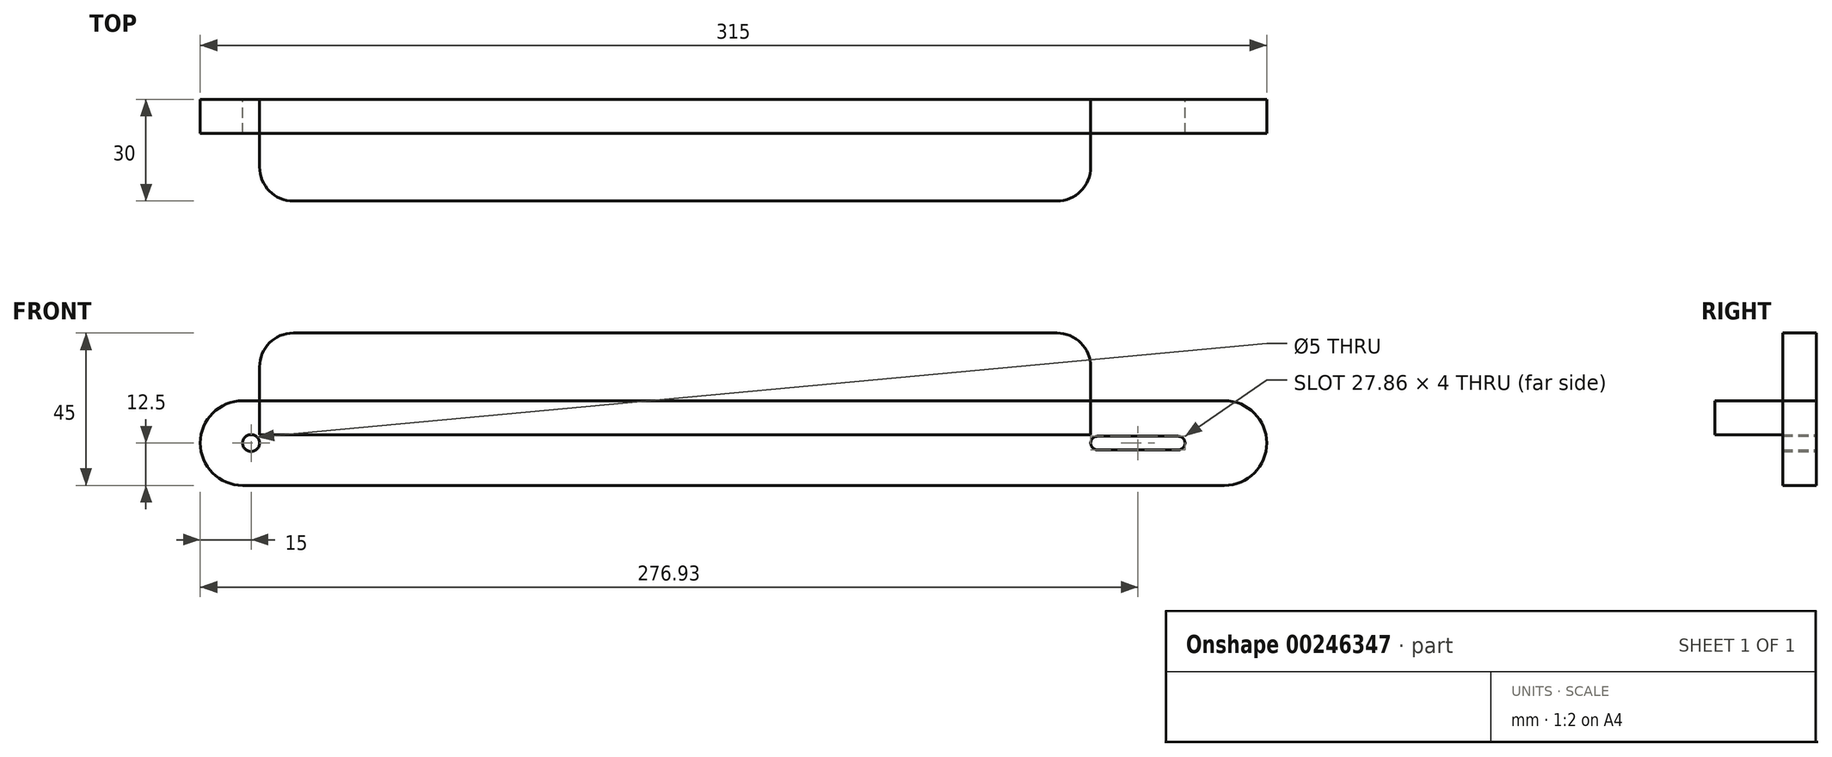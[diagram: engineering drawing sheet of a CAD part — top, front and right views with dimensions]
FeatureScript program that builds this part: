
annotation { "Feature Type Name" : "Feature", "Feature Type Description" : "" }
export const myFeature = defineFeature(function(context is Context, id is Id, definition is map)
    precondition{}
    {
        {
            var Q0;
            Q0=qCreatedBy(makeId("Front.planeOp"),FACE);
            var sketch = newSketch(context, id + "F0", { "sketchPlane" : qUnion([Q0])});
            skLineSegment(sketch, "E0.top", {"start": v(10, 25) * mm, "end": v(325, 25) * mm});
            skLineSegment(sketch, "E0.right", {"start": v(325, 0) * mm, "end": v(325, 25) * mm});
            skCircle(sketch, "E1", {"center": v(25, 12.5) * mm, "radius": 2.5 * mm});
            skArc(sketch, "E2", {"start": v(298.86, 10.5) * mm, "mid": v(300.86, 12.5) * mm, "end": v(298.86, 14.5) * mm});
            skArc(sketch, "E3", {"start": v(275, 14.5) * mm, "mid": v(273, 12.5) * mm, "end": v(275, 10.5) * mm});
            skLineSegment(sketch, "E4", {"start": v(275, 14.5) * mm, "end": v(298.86, 14.5) * mm});
            skLineSegment(sketch, "E5", {"start": v(298.86, 10.5) * mm, "end": v(275, 10.5) * mm});
            skLineSegment(sketch, "E6", {"start": v(325, 0) * mm, "end": v(10, 0) * mm});
            skLineSegment(sketch, "E7", {"start": v(10, 0) * mm, "end": v(10, 25) * mm});
            skSolve(sketch);
        }
        {
            var Q0;
            Q0 = qSketchRegion(id + "F0", true);
            extrude(context, id + "F1", {"entities" : qUnion([Q0]), "depth" : 10 * mm});
        }
        {
            var Q0;
            Q0=makeQuery(id+"F1.opExtrude","SWEPT_EDGE",EDGE,{"disambiguationData":[OSD([sQuery(id+"F0.wireOp",EDGE,"E0.top"),sQuery(id+"F0.wireOp",EDGE,"E7")])]});
            var Q1;
            Q1=makeQuery(id+"F1.opExtrude","SWEPT_EDGE",EDGE,{"disambiguationData":[OSD([sQuery(id+"F0.wireOp",EDGE,"E6"),sQuery(id+"F0.wireOp",EDGE,"E7")])]});
            var Q2;
            Q2=makeQuery(id+"F1.opExtrude","SWEPT_EDGE",EDGE,{"disambiguationData":[OSD([sQuery(id+"F0.wireOp",EDGE,"E0.right"),sQuery(id+"F0.wireOp",EDGE,"E6")])]});
            var Q3;
            Q3=makeQuery(id+"F1.opExtrude","SWEPT_EDGE",EDGE,{"disambiguationData":[OSD([sQuery(id+"F0.wireOp",EDGE,"E0.top"),sQuery(id+"F0.wireOp",EDGE,"E0.right")])]});
            fillet(context, id + "F2", {"entities" : qUnion([Q0, Q1, Q2, Q3]), "radius" : 12.5 * mm, "tangentPropagation" : true, "allowEdgeOverflow" : false});
        }
        {
            var Q0;
            Q0=makeQuery(id+"F1.opExtrude","CAP_FACE",FACE,{"disambiguationData":[OSD([sQuery(id+"F0.wireOp",EDGE,"E0.top"),sQuery(id+"F0.wireOp",EDGE,"E0.right"),sQuery(id+"F0.wireOp",EDGE,"E1"),sQuery(id+"F0.wireOp",EDGE,"E2"),sQuery(id+"F0.wireOp",EDGE,"E3"),sQuery(id+"F0.wireOp",EDGE,"E4"),sQuery(id+"F0.wireOp",EDGE,"E5"),sQuery(id+"F0.wireOp",EDGE,"E6"),sQuery(id+"F0.wireOp",EDGE,"E7")])],"isStart":false});
            var sketch = newSketch(context, id + "F3", { "sketchPlane" : qUnion([Q0])});
            skLineSegment(sketch, "E8", {"start": v(27.5, 15) * mm, "end": v(27.5, 25) * mm});
            skLineSegment(sketch, "E9", {"start": v(27.5, 25) * mm, "end": v(273, 25) * mm});
            skPoint(sketch, "E9.endSnap0", {"position": v(273, 12.5) * mm});
            skLineSegment(sketch, "E10", {"start": v(273, 25) * mm, "end": v(273, 15) * mm});
            skLineSegment(sketch, "E11", {"start": v(273, 15) * mm, "end": v(27.5, 15) * mm});
            skSolve(sketch);
        }
        {
            var Q0;
            Q0 = qSketchRegion(id + "F3", true);
            extrude(context, id + "F4", {"entities" : qUnion([Q0]), "operationType" : NewBodyOperationType.ADD, "depth" : 20 * mm});
        }
        {
            var Q0;
            Q0=makeQuery(id+"F4.boolean.opBoolean","MERGE",FACE,{"derivedFrom":[makeQuery(id+"F1.opExtrude","SWEPT_FACE",FACE,{"disambiguationData":[OSD([sQuery(id+"F0.wireOp",EDGE,"E0.top")])]}),makeQuery(id+"F4.opExtrude","SWEPT_FACE",FACE,{"disambiguationData":[OSD([sQuery(id+"F3.wireOp",EDGE,"E9")])]})]});
            var sketch = newSketch(context, id + "F5", { "sketchPlane" : qUnion([Q0])});
            skLineSegment(sketch, "E12", {"start": v(273, -10) * mm, "end": v(273, 0) * mm});
            skLineSegment(sketch, "E13", {"start": v(273, 0) * mm, "end": v(27.5, 0) * mm});
            skLineSegment(sketch, "E14", {"start": v(27.5, 0) * mm, "end": v(27.5, -10) * mm});
            skLineSegment(sketch, "E15", {"start": v(27.5, -10) * mm, "end": v(273, -10) * mm});
            skSolve(sketch);
        }
        {
            var Q0;
            Q0 = qSketchRegion(id + "F5", true);
            extrude(context, id + "F6", {"entities" : qUnion([Q0]), "operationType" : NewBodyOperationType.ADD, "depth" : 20 * mm});
        }
        {
            var Q0;
            Q0=makeQuery(id+"F6.opExtrude","CAP_EDGE",EDGE,{"disambiguationData":[OSD([sQuery(id+"F5.wireOp",EDGE,"E14")])],"isStart":false});
            fillet(context, id + "F7", {"entities" : qUnion([Q0]), "radius" : 10 * mm, "tangentPropagation" : true, "allowEdgeOverflow" : false});
        }
        {
            var Q0;
            Q0=makeQuery(id+"F6.opExtrude","CAP_EDGE",EDGE,{"disambiguationData":[OSD([sQuery(id+"F5.wireOp",EDGE,"E12")])],"isStart":false});
            var Q1;
            Q1=makeQuery(id+"F4.opExtrude","CAP_EDGE",EDGE,{"disambiguationData":[OSD([sQuery(id+"F3.wireOp",EDGE,"E10")])],"isStart":false});
            var Q2;
            Q2=makeQuery(id+"F4.opExtrude","CAP_EDGE",EDGE,{"disambiguationData":[OSD([sQuery(id+"F3.wireOp",EDGE,"E8")])],"isStart":false});
            fillet(context, id + "F8", {"entities" : qUnion([Q0, Q1, Q2]), "radius" : 10 * mm, "tangentPropagation" : true, "allowEdgeOverflow" : false});
        }
    });
